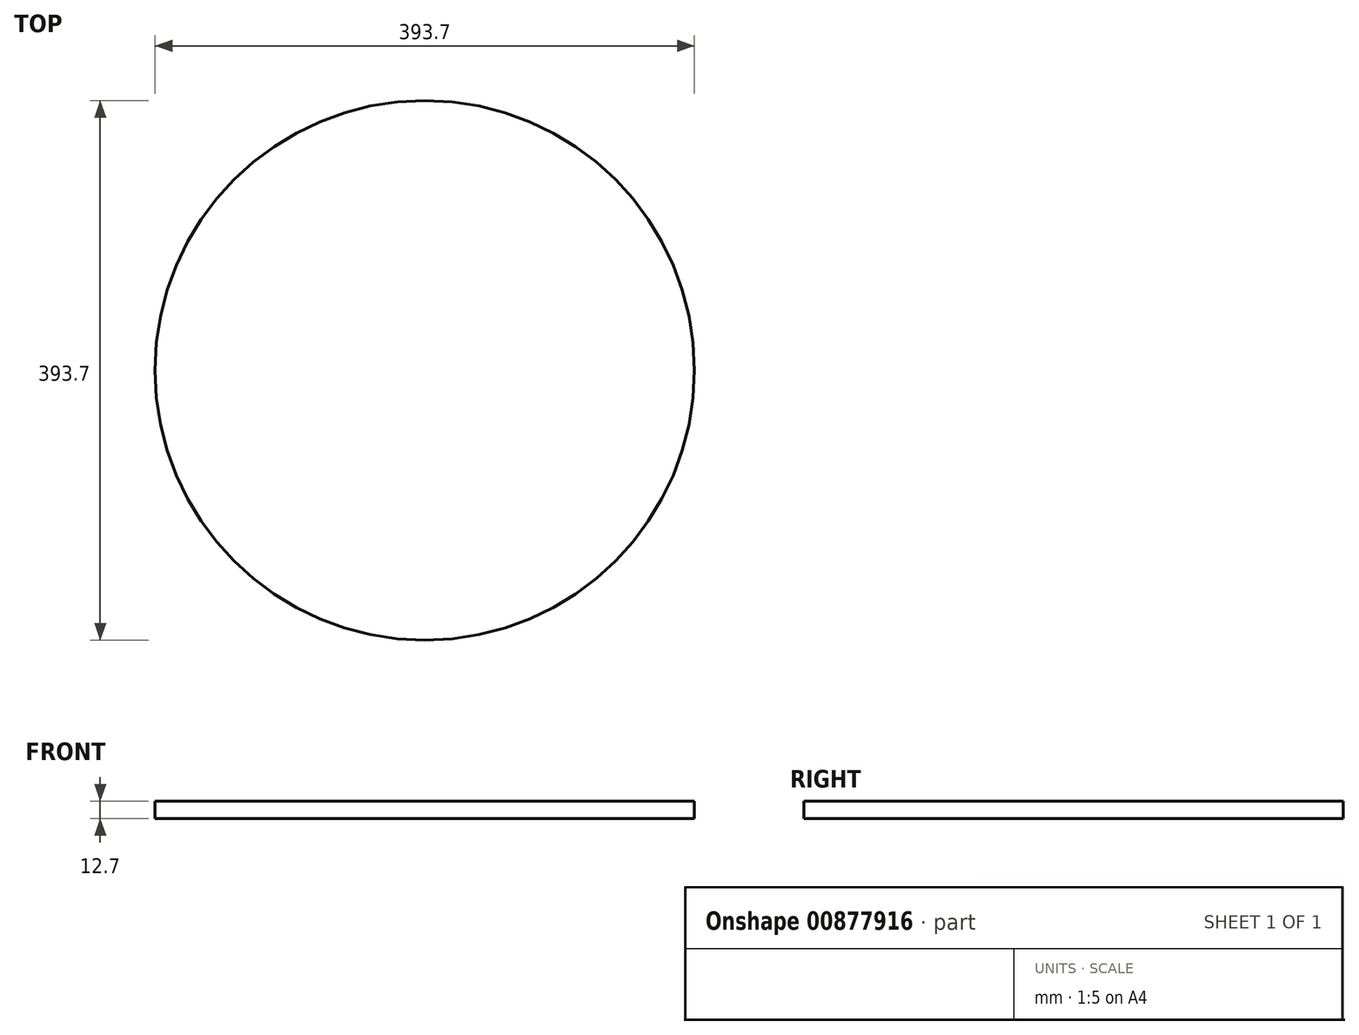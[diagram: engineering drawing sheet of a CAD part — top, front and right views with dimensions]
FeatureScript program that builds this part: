
annotation { "Feature Type Name" : "Feature", "Feature Type Description" : "" }
export const myFeature = defineFeature(function(context is Context, id is Id, definition is map)
    precondition{}
    {
        {
            var Q0;
            Q0=qCreatedBy(makeId("Top.planeOp"), FACE);
            var sketch = newSketch(context, id + "F0", { "sketchPlane" : qUnion([Q0])});
            skCircle(sketch, "E0", {"center": v(0, 0) * mm, "radius": 196.85 * mm});
            skSolve(sketch);
        }
        {
            var Q0;
            Q0 = qSketchRegion(id + "F0", true);
            extrude(context, id + "F1", {"entities" : qUnion([Q0]), "depth" : 12.7 * mm, "offsetDistance" : 25.4 * mm});
        }
    });
